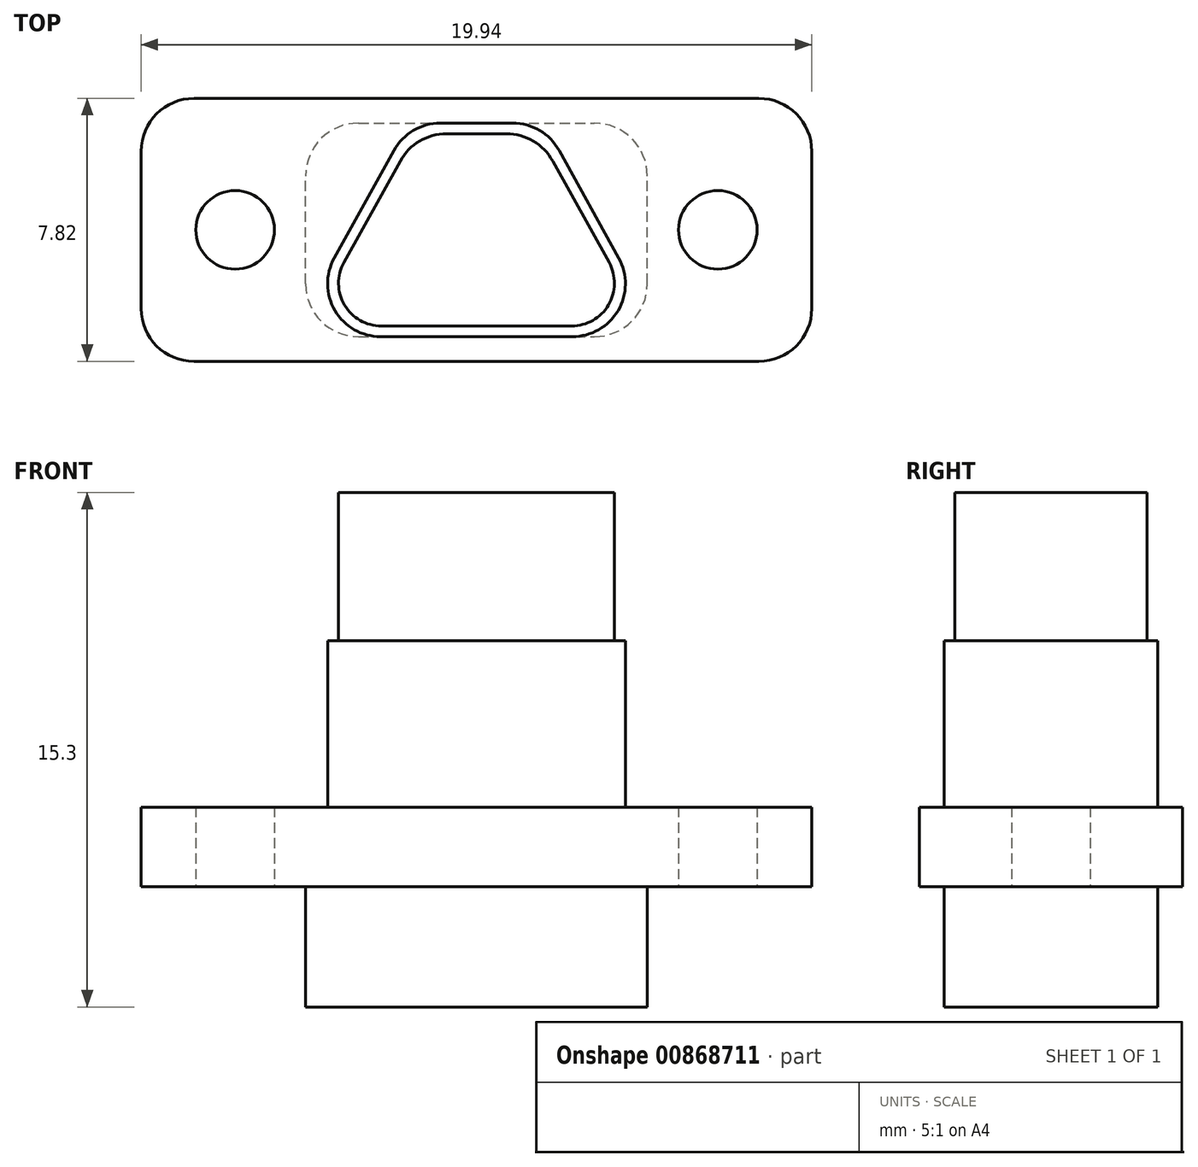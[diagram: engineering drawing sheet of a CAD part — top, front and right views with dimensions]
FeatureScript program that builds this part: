
annotation { "Feature Type Name" : "Feature", "Feature Type Description" : "" }
export const myFeature = defineFeature(function(context is Context, id is Id, definition is map)
    precondition{}
    {
        {
            var Q0;
            Q0=qCreatedBy(makeId("Top.planeOp"),FACE);
            var sketch = newSketch(context, id + "F0", { "sketchPlane" : qUnion([Q0])});
            skLineSegment(sketch, "E0.bottom", {"start": v(-8.4, 3.91) * mm, "end": v(8.4, 3.91) * mm});
            skLineSegment(sketch, "E0.top", {"start": v(-8.4, -3.91) * mm, "end": v(8.4, -3.91) * mm});
            skLineSegment(sketch, "E0.left", {"start": v(-9.97, 2.34) * mm, "end": v(-9.97, -2.34) * mm});
            skLineSegment(sketch, "E0.right", {"start": v(9.97, 2.34) * mm, "end": v(9.97, -2.34) * mm});
            skPoint(sketch, "E0.middle", {"position": v(0, 0) * mm});
            skCircle(sketch, "E1", {"center": v(-7.18, 0) * mm, "radius": 1.17 * mm});
            skCircle(sketch, "E2", {"center": v(7.18, 0) * mm, "radius": 1.17 * mm});
            skPoint(sketch, "E3.visualSharp", {"position": v(-9.97, -3.91) * mm});
            skArc(sketch, "E3.filletArc", {"start": v(-9.97, -2.34) * mm, "mid": v(-9.5, -3.45) * mm, "end": v(-8.4, -3.91) * mm});
            skPoint(sketch, "E4.visualSharp", {"position": v(-9.97, 3.91) * mm});
            skArc(sketch, "E4.filletArc", {"start": v(-8.4, 3.91) * mm, "mid": v(-9.5, 3.45) * mm, "end": v(-9.97, 2.34) * mm});
            skPoint(sketch, "E5.visualSharp", {"position": v(9.97, 3.91) * mm});
            skArc(sketch, "E5.filletArc", {"start": v(9.97, 2.34) * mm, "mid": v(9.5, 3.45) * mm, "end": v(8.4, 3.91) * mm});
            skPoint(sketch, "E6.visualSharp", {"position": v(9.97, -3.91) * mm});
            skArc(sketch, "E6.filletArc", {"start": v(8.4, -3.91) * mm, "mid": v(9.5, -3.45) * mm, "end": v(9.97, -2.34) * mm});
            skSolve(sketch);
        }
        {
            var Q0;
            Q0=makeQuery(id+"F0.imprint","IMPRINT",FACE,{"disambiguationData":[TD([[makeQuery(id+"F0.imprint","IMPRINT",EDGE,{"derivedFrom":sQuery(id+"F0.wireOp",EDGE,"E0.bottom")}),-1.0]])]});
            extrude(context, id + "F1", {"entities" : qUnion([Q0]), "endBound" : BoundingType.SYMMETRIC, "depth" : 2.36 * mm, "offsetDistance" : 25.4 * mm});
        }
        {
            var Q0;
            Q0=makeQuery(id+"F1.opExtrude","CAP_FACE",FACE,{"disambiguationData":[OSD([sQuery(id+"F0.wireOp",EDGE,"E0.bottom"),sQuery(id+"F0.wireOp",EDGE,"E0.top"),sQuery(id+"F0.wireOp",EDGE,"E0.left"),sQuery(id+"F0.wireOp",EDGE,"E0.right"),sQuery(id+"F0.wireOp",EDGE,"E1"),sQuery(id+"F0.wireOp",EDGE,"E2"),sQuery(id+"F0.wireOp",EDGE,"E3.filletArc"),sQuery(id+"F0.wireOp",EDGE,"E4.filletArc"),sQuery(id+"F0.wireOp",EDGE,"E5.filletArc"),sQuery(id+"F0.wireOp",EDGE,"E6.filletArc")])],"isStart":false});
            var sketch = newSketch(context, id + "F2", { "sketchPlane" : qUnion([Q0])});
            skPoint(sketch, "E7.middle", {"position": v(0, 0) * mm});
            skLineSegment(sketch, "E8.top", {"start": v(2.85, -3.17) * mm, "end": v(-2.85, -3.17) * mm});
            skLineSegment(sketch, "E9", {"start": v(-1.08, 3.18) * mm, "end": v(1.08, 3.18) * mm});
            skLineSegment(sketch, "E10", {"start": v(-4.23, -0.84) * mm, "end": v(-2.45, 2.36) * mm});
            skLineSegment(sketch, "E11", {"start": v(2.46, 2.36) * mm, "end": v(4.23, -0.84) * mm});
            skPoint(sketch, "E12.visualSharp", {"position": v(-2, 3.18) * mm});
            skArc(sketch, "E12.filletArc", {"start": v(-1.08, 3.18) * mm, "mid": v(-1.88, 2.96) * mm, "end": v(-2.45, 2.36) * mm});
            skPoint(sketch, "E13.visualSharp", {"position": v(-5.52, -3.17) * mm});
            skArc(sketch, "E13.filletArc", {"start": v(-4.23, -0.84) * mm, "mid": v(-4.2, -2.4) * mm, "end": v(-2.85, -3.17) * mm});
            skPoint(sketch, "E14.visualSharp", {"position": v(5.53, -3.17) * mm});
            skArc(sketch, "E14.filletArc", {"start": v(2.85, -3.17) * mm, "mid": v(4.2, -2.4) * mm, "end": v(4.23, -0.84) * mm});
            skPoint(sketch, "E15.visualSharp", {"position": v(2, 3.18) * mm});
            skArc(sketch, "E15.filletArc", {"start": v(2.46, 2.36) * mm, "mid": v(1.88, 2.96) * mm, "end": v(1.08, 3.18) * mm});
            skSolve(sketch);
        }
        {
            var Q0;
            Q0=qSketchRegion(id+"F2",true);
            extrude(context, id + "F3", {"entities" : qUnion([Q0]), "operationType" : NewBodyOperationType.ADD, "depth" : 4.95 * mm, "offsetDistance" : 25.4 * mm});
        }
        {
            var Q0;
            Q0=makeQuery(id+"F1.opExtrude","CAP_FACE",FACE,{"disambiguationData":[OSD([sQuery(id+"F0.wireOp",EDGE,"E0.bottom"),sQuery(id+"F0.wireOp",EDGE,"E0.top"),sQuery(id+"F0.wireOp",EDGE,"E0.left"),sQuery(id+"F0.wireOp",EDGE,"E0.right"),sQuery(id+"F0.wireOp",EDGE,"E1"),sQuery(id+"F0.wireOp",EDGE,"E2"),sQuery(id+"F0.wireOp",EDGE,"E3.filletArc"),sQuery(id+"F0.wireOp",EDGE,"E4.filletArc"),sQuery(id+"F0.wireOp",EDGE,"E5.filletArc"),sQuery(id+"F0.wireOp",EDGE,"E6.filletArc")])],"isStart":true});
            var sketch = newSketch(context, id + "F4", { "sketchPlane" : qUnion([Q0])});
            skLineSegment(sketch, "E16.bottom", {"start": v(-3.5, 3.18) * mm, "end": v(3.5, 3.18) * mm});
            skLineSegment(sketch, "E16.top", {"start": v(-3.5, -3.18) * mm, "end": v(3.5, -3.18) * mm});
            skLineSegment(sketch, "E16.left", {"start": v(-5.08, 1.6) * mm, "end": v(-5.08, -1.6) * mm});
            skLineSegment(sketch, "E16.right", {"start": v(5.08, 1.6) * mm, "end": v(5.08, -1.6) * mm});
            skPoint(sketch, "E16.middle", {"position": v(0, 0) * mm});
            skPoint(sketch, "E17.visualSharp", {"position": v(-5.08, 3.17) * mm});
            skArc(sketch, "E17.filletArc", {"start": v(-3.5, 3.18) * mm, "mid": v(-4.62, 2.71) * mm, "end": v(-5.08, 1.6) * mm});
            skPoint(sketch, "E18.visualSharp", {"position": v(-5.08, -3.18) * mm});
            skArc(sketch, "E18.filletArc", {"start": v(-5.08, -1.6) * mm, "mid": v(-4.62, -2.71) * mm, "end": v(-3.5, -3.17) * mm});
            skPoint(sketch, "E19.visualSharp", {"position": v(5.08, -3.18) * mm});
            skArc(sketch, "E19.filletArc", {"start": v(3.5, -3.18) * mm, "mid": v(4.62, -2.71) * mm, "end": v(5.08, -1.6) * mm});
            skPoint(sketch, "E20.visualSharp", {"position": v(5.08, 3.18) * mm});
            skArc(sketch, "E20.filletArc", {"start": v(5.08, 1.6) * mm, "mid": v(4.62, 2.71) * mm, "end": v(3.5, 3.18) * mm});
            skSolve(sketch);
        }
        {
            var Q0;
            Q0=qSketchRegion(id+"F4",true);
            extrude(context, id + "F5", {"entities" : qUnion([Q0]), "operationType" : NewBodyOperationType.ADD, "depth" : 3.58 * mm, "offsetDistance" : 25.4 * mm});
        }
        {
            var Q0;
            Q0=makeQuery(id+"F3.opExtrude","CAP_FACE",FACE,{"disambiguationData":[OSD([sQuery(id+"F2.wireOp",EDGE,"E8.top"),sQuery(id+"F2.wireOp",EDGE,"E9"),sQuery(id+"F2.wireOp",EDGE,"E10"),sQuery(id+"F2.wireOp",EDGE,"E11"),sQuery(id+"F2.wireOp",EDGE,"E12.filletArc"),sQuery(id+"F2.wireOp",EDGE,"E13.filletArc"),sQuery(id+"F2.wireOp",EDGE,"E14.filletArc"),sQuery(id+"F2.wireOp",EDGE,"E15.filletArc")])],"isStart":false});
            var sketch = newSketch(context, id + "F6", { "sketchPlane" : qUnion([Q0])});
            skLineSegment(sketch, "E21", {"start": v(-0.89, 2.86) * mm, "end": v(0.9, 2.86) * mm});
            skLineSegment(sketch, "E22", {"start": v(2.27, 2.05) * mm, "end": v(3.94, -0.97) * mm});
            skLineSegment(sketch, "E23", {"start": v(2.83, -2.86) * mm, "end": v(-2.83, -2.86) * mm});
            skLineSegment(sketch, "E24", {"start": v(-3.94, -0.97) * mm, "end": v(-2.27, 2.05) * mm});
            skPoint(sketch, "E25.visualSharp", {"position": v(-4.99, -2.86) * mm});
            skArc(sketch, "E25.filletArc", {"start": v(-3.94, -0.97) * mm, "mid": v(-3.92, -2.23) * mm, "end": v(-2.83, -2.86) * mm});
            skPoint(sketch, "E26.visualSharp", {"position": v(-1.82, 2.86) * mm});
            skArc(sketch, "E26.filletArc", {"start": v(-0.89, 2.86) * mm, "mid": v(-1.69, 2.64) * mm, "end": v(-2.27, 2.05) * mm});
            skPoint(sketch, "E27.visualSharp", {"position": v(1.82, 2.86) * mm});
            skArc(sketch, "E27.filletArc", {"start": v(2.27, 2.05) * mm, "mid": v(1.7, 2.64) * mm, "end": v(0.9, 2.86) * mm});
            skPoint(sketch, "E28.visualSharp", {"position": v(4.99, -2.86) * mm});
            skArc(sketch, "E28.filletArc", {"start": v(2.83, -2.86) * mm, "mid": v(3.93, -2.23) * mm, "end": v(3.94, -0.97) * mm});
            skSolve(sketch);
        }
        {
            var Q0;
            Q0=qSketchRegion(id+"F6",true);
            extrude(context, id + "F7", {"entities" : qUnion([Q0]), "operationType" : NewBodyOperationType.ADD, "oppositeDirection" : true, "depth" : -4.4 * mm, "offsetDistance" : 25.4 * mm});
        }
    });
